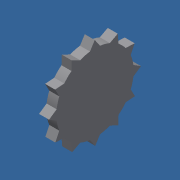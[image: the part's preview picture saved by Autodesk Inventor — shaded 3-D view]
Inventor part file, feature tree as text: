
AUTODESK INVENTOR PART (.ipt)
format: ipt  version: 2018 (Build 220112000, 112)  size: 116,224 bytes
history: native  units: mm
features: extrude x1, sketch x1
ambient origin geometry x8: Origin, YZ Plane, XZ Plane, XY Plane, X Axis, Y Axis, Z Axis, Center Point
bodies: Solid1 (feature_tree)
feature tree (2):
  extrude  "Extrusion1"  Depth=6.0mm TaperAngle=0.0deg
  sketch  "Sketch1"  dims[d0=120.0mm d2=360.0deg d4=6.0mm d5=0.0mm]
